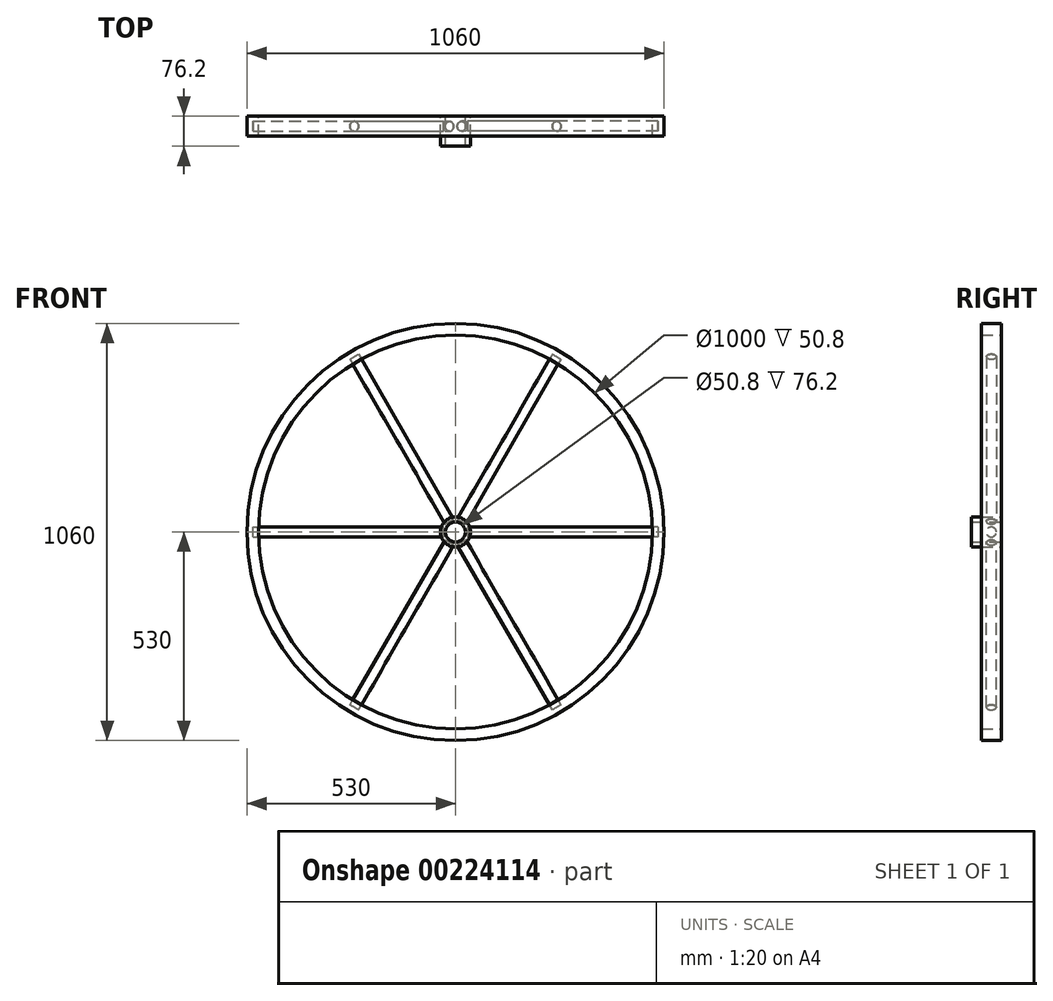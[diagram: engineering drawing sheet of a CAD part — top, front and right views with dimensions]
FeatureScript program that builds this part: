
annotation { "Feature Type Name" : "Feature", "Feature Type Description" : "" }
export const myFeature = defineFeature(function(context is Context, id is Id, definition is map)
    precondition{}
    {
        {
            var Q0;
            Q0=qCreatedBy(makeId("Front.planeOp"),FACE);
            var sketch = newSketch(context, id + "F0", { "sketchPlane" : qUnion([Q0])});
            skCircle(sketch, "E0", {"center": v(0, 0) * mm, "radius": 25.4 * mm});
            skCircle(sketch, "E1", {"center": v(0, 0) * mm, "radius": 38.1 * mm});
            skCircle(sketch, "E2", {"center": v(0, 0) * mm, "radius": 500 * mm});
            skCircle(sketch, "E3", {"center": v(0, 0) * mm, "radius": 530 * mm});
            skLineSegment(sketch, "E4", {"start": v(35.92, 12.7) * mm, "end": v(499.84, 12.7) * mm});
            skLineSegment(sketch, "E5", {"start": v(38.1, 0) * mm, "end": v(500, 0) * mm, "construction": true});
            skLineSegment(sketch, "E6", {"start": v(296.24, 12.7) * mm, "end": v(296.24, 0) * mm});
            skLineSegment(sketch, "E7", {"start": v(35.92, -12.7) * mm, "end": v(499.84, -12.7) * mm});
            skLineSegment(sketch, "E8", {"start": v(269.05, 0) * mm, "end": v(269.05, -12.7) * mm});
            skArc(sketch, "E9", {"start": v(-530, 0) * mm, "mid": v(-529.01, 32.34) * mm, "end": v(-526.05, 64.56) * mm});
            skSolve(sketch);
        }
        {
            var Q0;
            Q0=makeQuery(id+"F0.imprint","IMPRINT",FACE,{"disambiguationData":[TD([[makeQuery(id+"F0.imprint","IMPRINT",EDGE,{"derivedFrom":sQuery(id+"F0.wireOp",EDGE,"E0")}),-1.0]])]});
            var Q1;
            Q1=sQuery(id+"F0.wireOp",EDGE,"E1");
            var Q2;
            Q2=sQuery(id+"F0.wireOp",EDGE,"E0");
            extrude(context, id + "F1", {"entities" : qUnion([Q0]), "surfaceEntities" : qUnion([Q1, Q2]), "depth" : 76.2 * mm});
        }
        {
            var Q0;
            Q0 = qSketchRegion(id + "F0", true);
            extrude(context, id + "F2", {"entities" : qUnion([Q0]), "depth" : 50.8 * mm});
        }
        {
            var Q0;
            Q0=qCreatedBy(makeId("Right.planeOp"),FACE);
            var sketch = newSketch(context, id + "F3", { "sketchPlane" : qUnion([Q0])});
            skLineSegment(sketch, "E10", {"start": v(0, 0) * mm, "end": v(-91.02, 0) * mm});
            skSolve(sketch);
        }
        {
            var Q0;
            Q0=qCreatedBy(makeId("Front.planeOp"),FACE);
            cPlane(context, id + "F4", {"entities" : qUnion([Q0]), "cplaneType" : CPlaneType.OFFSET, "offset" : 25.4 * mm, "width" : 152.4 * mm, "height" : 152.4 * mm});
        }
        {
            var Q0;
            Q0=qCreatedBy(id+"F4.planeOp",FACE);
            var sketch = newSketch(context, id + "F5", { "sketchPlane" : qUnion([Q0])});
            skLineSegment(sketch, "E11", {"start": v(503.67, -12.7) * mm, "end": v(34.27, -12.7) * mm});
            skLineSegment(sketch, "E12", {"start": v(503.67, 12.7) * mm, "end": v(30.9, 12.7) * mm});
            skLineSegment(sketch, "E13", {"start": v(503.67, -12.7) * mm, "end": v(514.31, -12.7) * mm});
            skLineSegment(sketch, "E14", {"start": v(514.31, -12.7) * mm, "end": v(514.31, 12.7) * mm});
            skLineSegment(sketch, "E15", {"start": v(514.31, 12.7) * mm, "end": v(503.67, 12.7) * mm});
            skLineSegment(sketch, "E16", {"start": v(30.9, 12.7) * mm, "end": v(30.9, -13.77) * mm});
            skLineSegment(sketch, "E17", {"start": v(34.27, -12.7) * mm, "end": v(30.9, -12.7) * mm});
            skPoint(sketch, "E18.endSnap0", {"position": v(514.31, 0) * mm});
            skLineSegment(sketch, "E19", {"start": v(0, 0) * mm, "end": v(967.05, 0) * mm});
            skSolve(sketch);
        }
        {
            var Q0;
            {var subQ1=sQuery(id+"F5.wireOp",EDGE,"E12");Q0=makeQuery(id+"F5.imprint","IMPRINT",FACE,{"disambiguationData":[TD([[makeQuery(id+"F5.imprint","IMPRINT",EDGE,{"derivedFrom":subQ1}),1.0]])]});}
            var Q1;
            Q1=sQuery(id+"F5.wireOp",EDGE,"E12");
            var Q2;
            Q2=sQuery(id+"F5.wireOp",EDGE,"E11");
            var Q3;
            Q3=sQuery(id+"F5.wireOp",EDGE,"E19");
            revolve(context, id + "F6", {"entities" : qUnion([Q0]), "surfaceEntities" : qUnion([Q1, Q2]), "axis" : qUnion([Q3]), "revolveType" : RevolveType.FULL});
        }
        {
            var Q0;
            Q0=makeQuery(id+"F6.opRevolve","SWEPT_BODY",BODY,{"disambiguationData":[OSD([sQuery(id+"F5.wireOp",EDGE,"E12"),sQuery(id+"F5.wireOp",EDGE,"E14"),sQuery(id+"F5.wireOp",EDGE,"E15"),sQuery(id+"F5.wireOp",EDGE,"E16"),sQuery(id+"F5.wireOp",EDGE,"E19")])]});
            var Q1;
            Q1=sQuery(id+"F3.wireOp",EDGE,"E10");
            circularPattern(context, id + "F7", {"entities" : qUnion([Q0]), "axis" : qUnion([Q1]), "angle" : 360 * degree, "instanceCount" : 6, "equalSpace" : true});
        }
    });
